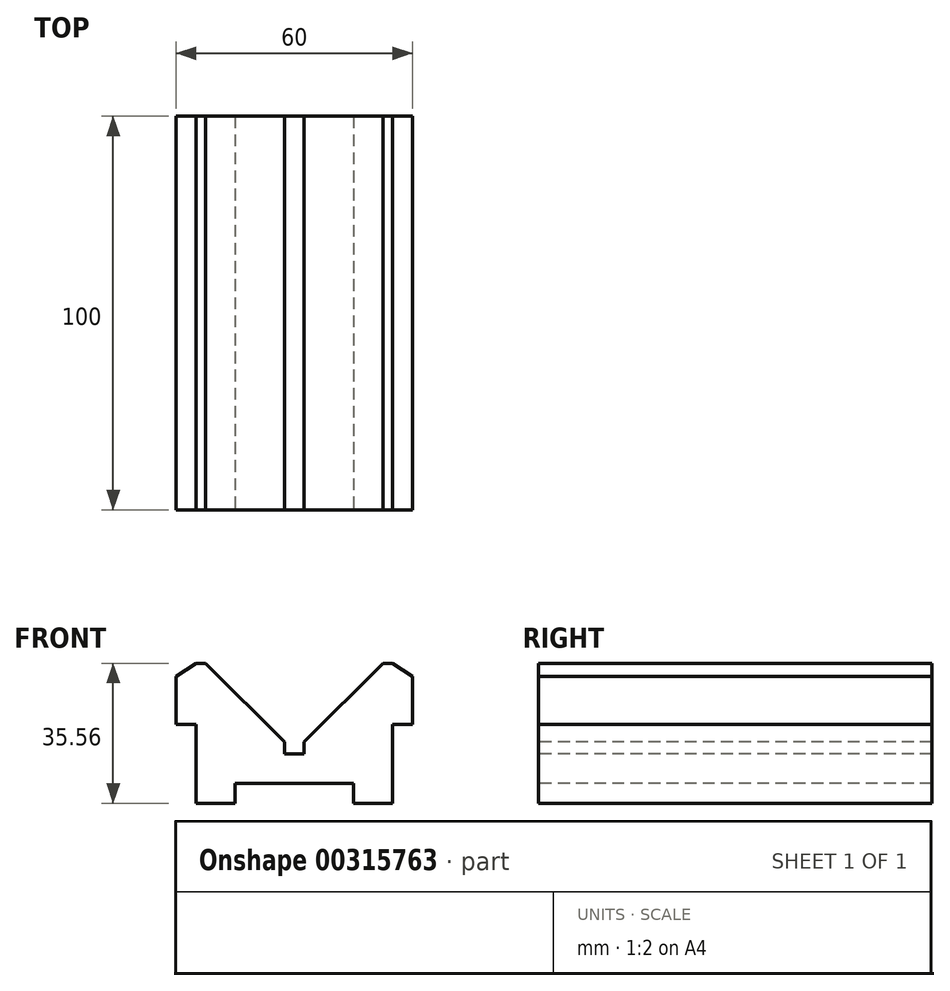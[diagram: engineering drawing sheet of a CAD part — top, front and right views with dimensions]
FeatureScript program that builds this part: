
annotation { "Feature Type Name" : "Feature", "Feature Type Description" : "" }
export const myFeature = defineFeature(function(context is Context, id is Id, definition is map)
    precondition{}
    {
        {
            var Q0;
            Q0=qCreatedBy(makeId("Front.planeOp"),FACE);
            var sketch = newSketch(context, id + "F0", { "sketchPlane" : qUnion([Q0])});
            skLineSegment(sketch, "E0", {"start": v(-5, 6.11) * mm, "end": v(-5, 3.11) * mm});
            skLineSegment(sketch, "E1", {"start": v(-5, 3.11) * mm, "end": v(0, 3.11) * mm});
            skLineSegment(sketch, "E2", {"start": v(0, 3.11) * mm, "end": v(0, 6.11) * mm});
            skLineSegment(sketch, "E3", {"start": v(22.5, 26.11) * mm, "end": v(27.5, 22.8) * mm});
            skLineSegment(sketch, "E4", {"start": v(27.5, 22.8) * mm, "end": v(27.5, 10.55) * mm});
            skLineSegment(sketch, "E5", {"start": v(27.5, 10.55) * mm, "end": v(22.5, 10.55) * mm});
            skLineSegment(sketch, "E6", {"start": v(22.5, 10.55) * mm, "end": v(22.5, -9.45) * mm});
            skLineSegment(sketch, "E7", {"start": v(22.5, -9.45) * mm, "end": v(12.5, -9.45) * mm});
            skLineSegment(sketch, "E8", {"start": v(12.5, -9.45) * mm, "end": v(12.5, -4.45) * mm});
            skLineSegment(sketch, "E9", {"start": v(12.5, -4.45) * mm, "end": v(-17.5, -4.45) * mm});
            skLineSegment(sketch, "E10", {"start": v(-17.5, -4.45) * mm, "end": v(-17.5, -9.45) * mm});
            skLineSegment(sketch, "E11", {"start": v(-17.5, -9.45) * mm, "end": v(-27.5, -9.45) * mm});
            skLineSegment(sketch, "E12", {"start": v(-27.5, -9.45) * mm, "end": v(-27.5, 10.55) * mm});
            skLineSegment(sketch, "E13", {"start": v(-27.5, 10.55) * mm, "end": v(-32.5, 10.55) * mm});
            skLineSegment(sketch, "E14", {"start": v(-32.5, 10.55) * mm, "end": v(-32.5, 22.8) * mm});
            skLineSegment(sketch, "E15", {"start": v(-32.5, 22.8) * mm, "end": v(-27.5, 26.11) * mm});
            skLineSegment(sketch, "E16", {"start": v(-27.5, 26.11) * mm, "end": v(-25, 26.11) * mm});
            skLineSegment(sketch, "E17", {"start": v(-25, 26.11) * mm, "end": v(-5, 6.11) * mm});
            skLineSegment(sketch, "E18", {"start": v(22.5, 26.11) * mm, "end": v(20, 26.11) * mm});
            skLineSegment(sketch, "E19", {"start": v(20, 26.11) * mm, "end": v(0, 6.11) * mm});
            skSolve(sketch);
        }
        {
            var Q0;
            Q0=makeQuery(id+"F0.imprint","IMPRINT",FACE,{"disambiguationData":[TD([[makeQuery(id+"F0.imprint","IMPRINT",EDGE,{"derivedFrom":sQuery(id+"F0.wireOp",EDGE,"E0")}),-1.0]])]});
            extrude(context, id + "F1", {"entities" : qUnion([Q0]), "oppositeDirection" : true, "depth" : 100 * mm});
        }
    });
